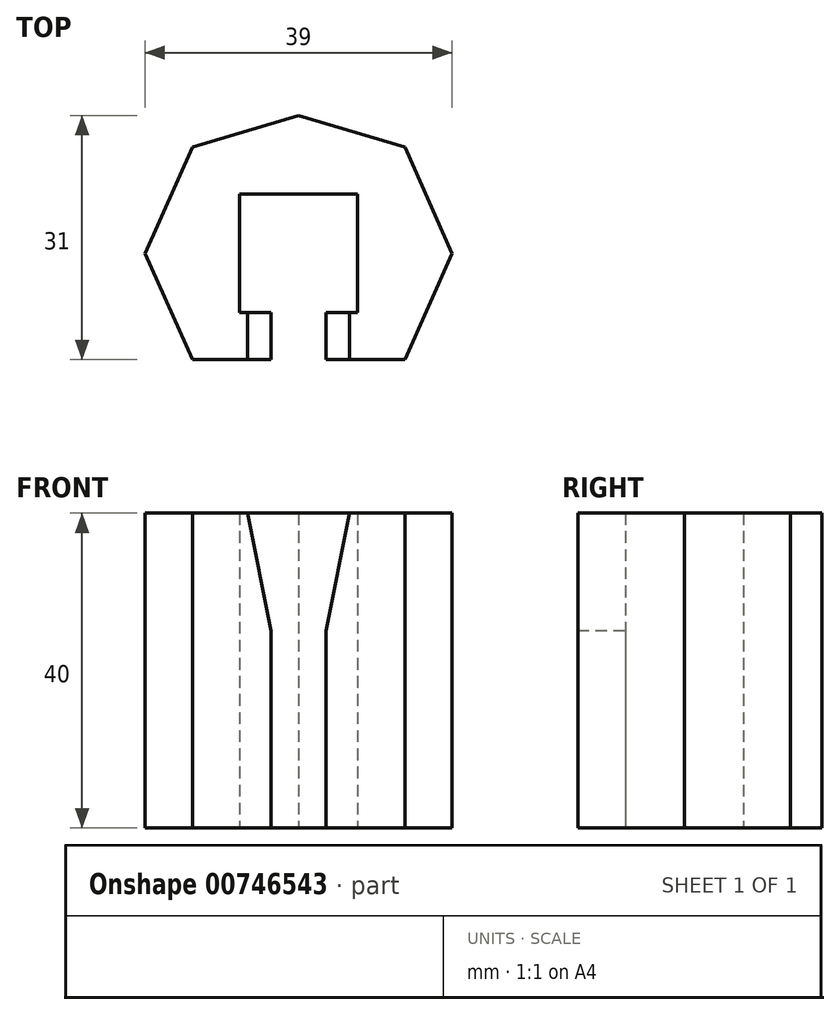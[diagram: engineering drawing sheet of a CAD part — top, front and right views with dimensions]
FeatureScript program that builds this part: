
annotation { "Feature Type Name" : "Feature", "Feature Type Description" : "" }
export const myFeature = defineFeature(function(context is Context, id is Id, definition is map)
    precondition{}
    {
        {
            var Q0;
            Q0=qCreatedBy(makeId("Top.planeOp"),FACE);
            var sketch = newSketch(context, id + "F0", { "sketchPlane" : qUnion([Q0])});
            skLineSegment(sketch, "E0", {"start": v(-7.5, 7.5) * mm, "end": v(-7.5, -7.5) * mm});
            skLineSegment(sketch, "E1", {"start": v(-7.5, -7.5) * mm, "end": v(7.5, -7.5) * mm, "construction": true});
            skLineSegment(sketch, "E2", {"start": v(-7.5, 7.5) * mm, "end": v(7.5, 7.5) * mm, "construction": true});
            skLineSegment(sketch, "E3", {"start": v(7.5, 7.5) * mm, "end": v(7.5, -7.5) * mm});
            skLineSegment(sketch, "E4", {"start": v(-7.5, 7.5) * mm, "end": v(-7.5, 7.5) * mm});
            skLineSegment(sketch, "E5", {"start": v(-7.5, 7.5) * mm, "end": v(7.5, 7.5) * mm});
            skLineSegment(sketch, "E6", {"start": v(7.5, 7.5) * mm, "end": v(7.5, 7.5) * mm});
            skLineSegment(sketch, "E7", {"start": v(-7.5, -7.5) * mm, "end": v(-3.5, -7.5) * mm});
            skLineSegment(sketch, "E8", {"start": v(7.5, -7.5) * mm, "end": v(3.5, -7.5) * mm});
            skLineSegment(sketch, "E9", {"start": v(-3.5, -7.5) * mm, "end": v(3.5, -7.5) * mm, "construction": true});
            skLineSegment(sketch, "E10", {"start": v(-3.5, -7.5) * mm, "end": v(-3.5, -13.5) * mm});
            skLineSegment(sketch, "E11", {"start": v(-3.5, -13.5) * mm, "end": v(-13.5, -13.5) * mm});
            skLineSegment(sketch, "E12", {"start": v(3.5, -7.5) * mm, "end": v(3.5, -13.5) * mm});
            skLineSegment(sketch, "E13", {"start": v(3.5, -13.5) * mm, "end": v(13.5, -13.5) * mm});
            skLineSegment(sketch, "E14", {"start": v(-13.5, -13.5) * mm, "end": v(-19.5, 0) * mm});
            skLineSegment(sketch, "E15", {"start": v(-19.5, 0) * mm, "end": v(-13.5, 13.5) * mm});
            skLineSegment(sketch, "E16", {"start": v(-13.5, 13.5) * mm, "end": v(13.5, 13.5) * mm, "construction": true});
            skLineSegment(sketch, "E17", {"start": v(13.5, 13.5) * mm, "end": v(19.5, 0) * mm});
            skLineSegment(sketch, "E18", {"start": v(19.5, 0) * mm, "end": v(13.5, -13.5) * mm});
            skLineSegment(sketch, "E19", {"start": v(19.5, 0) * mm, "end": v(13.5, 0) * mm, "construction": true});
            skLineSegment(sketch, "E20", {"start": v(-19.5, 0) * mm, "end": v(-13.5, 0) * mm, "construction": true});
            skLineSegment(sketch, "E21", {"start": v(-13.5, 0) * mm, "end": v(-13.5, -13.5) * mm, "construction": true});
            skLineSegment(sketch, "E22", {"start": v(-13.5, 0) * mm, "end": v(-13.5, 13.5) * mm, "construction": true});
            skLineSegment(sketch, "E23", {"start": v(13.5, -13.5) * mm, "end": v(13.5, 0) * mm, "construction": true});
            skLineSegment(sketch, "E24", {"start": v(13.5, 13.5) * mm, "end": v(13.5, 0) * mm, "construction": true});
            skLineSegment(sketch, "E25", {"start": v(0, 7.5) * mm, "end": v(0, 13.5) * mm, "construction": true});
            skLineSegment(sketch, "E26", {"start": v(-7.5, 0) * mm, "end": v(-13.5, 0) * mm, "construction": true});
            skLineSegment(sketch, "E27", {"start": v(-13.5, 13.5) * mm, "end": v(0, 17.5) * mm});
            skLineSegment(sketch, "E28", {"start": v(0, 17.5) * mm, "end": v(13.5, 13.5) * mm});
            skLineSegment(sketch, "E29", {"start": v(0, 17.5) * mm, "end": v(0, 13.5) * mm, "construction": true});
            skLineSegment(sketch, "E30", {"start": v(-3.5, -13.5) * mm, "end": v(3.5, -13.5) * mm, "construction": true});
            skLineSegment(sketch, "E31", {"start": v(-13.5, -13.5) * mm, "end": v(0, -17.5) * mm, "construction": true});
            skLineSegment(sketch, "E32", {"start": v(0, -17.5) * mm, "end": v(13.5, -13.5) * mm, "construction": true});
            skLineSegment(sketch, "E33", {"start": v(0, -17.5) * mm, "end": v(0, -13.5) * mm, "construction": true});
            skLineSegment(sketch, "E34", {"start": v(0, 17.5) * mm, "end": v(0, -17.5) * mm, "construction": true});
            skLineSegment(sketch, "E35", {"start": v(-19.5, 0) * mm, "end": v(19.5, 0) * mm, "construction": true});
            skPoint(sketch, "E36", {"position": v(0, 0) * mm});
            skLineSegment(sketch, "E37", {"start": v(7.5, 7.5) * mm, "end": v(7.5, 13.5) * mm, "construction": true});
            skSolve(sketch);
        }
        {
            var Q0;
            Q0=makeQuery(id+"F0.imprint","IMPRINT",FACE,{"disambiguationData":[TD([[makeQuery(id+"F0.imprint","IMPRINT",EDGE,{"derivedFrom":sQuery(id+"F0.wireOp",EDGE,"E0")}),-1.0]])]});
            extrude(context, id + "F1", {"entities" : qUnion([Q0]), "depth" : 40 * mm, "offsetDistance" : 25 * mm});
        }
        {
            var Q0;
            Q0=makeQuery(id+"F1.opExtrude","SWEPT_FACE",FACE,{"disambiguationData":[OSD([sQuery(id+"F0.wireOp",EDGE,"E11")])]});
            var sketch = newSketch(context, id + "F2", { "sketchPlane" : qUnion([Q0])});
            skLineSegment(sketch, "E38", {"start": v(-3.5, 40) * mm, "end": v(-6.5, 40) * mm});
            skLineSegment(sketch, "E39", {"start": v(-6.5, 40) * mm, "end": v(-3.5, 25) * mm});
            skLineSegment(sketch, "E40", {"start": v(-3.5, 25) * mm, "end": v(-3.5, 40) * mm});
            skLineSegment(sketch, "E41", {"start": v(6.5, 40) * mm, "end": v(3.5, 25) * mm});
            skLineSegment(sketch, "E42", {"start": v(3.5, 25) * mm, "end": v(3.5, 40) * mm});
            skLineSegment(sketch, "E43", {"start": v(3.5, 40) * mm, "end": v(6.5, 40) * mm});
            skLineSegment(sketch, "E44", {"start": v(-3.5, 40) * mm, "end": v(3.5, 40) * mm, "construction": true});
            skSolve(sketch);
        }
        {
            var Q0;
            Q0 = qSketchRegion(id + "F2", true);
            extrude(context, id + "F3", {"entities" : qUnion([Q0]), "operationType" : NewBodyOperationType.REMOVE, "oppositeDirection" : true, "depth" : 6 * mm, "offsetDistance" : 25 * mm});
        }
    });
